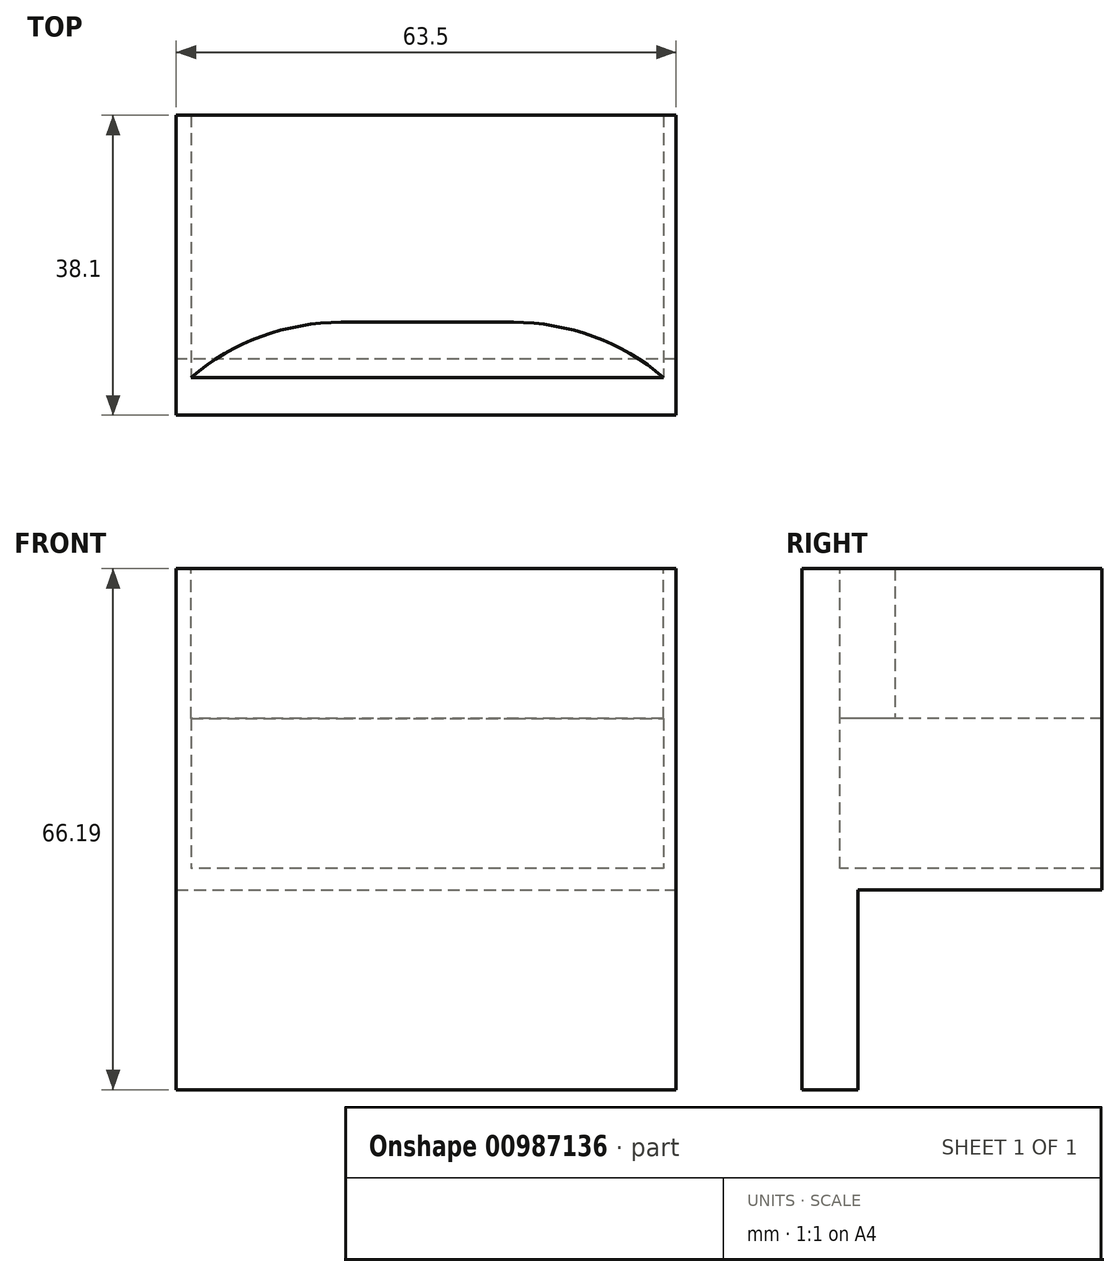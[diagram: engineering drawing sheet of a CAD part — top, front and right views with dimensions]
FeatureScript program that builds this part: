
annotation { "Feature Type Name" : "Feature", "Feature Type Description" : "" }
export const myFeature = defineFeature(function(context is Context, id is Id, definition is map)
    precondition{}
    {
        {
            var Q0;
            Q0=qCreatedBy(makeId("Top.planeOp"),FACE);
            var sketch = newSketch(context, id + "F0", { "sketchPlane" : qUnion([Q0])});
            skLineSegment(sketch, "E0.bottom", {"start": v(-32.48, 36.7) * mm, "end": v(31.02, 36.7) * mm});
            skLineSegment(sketch, "E0.top", {"start": v(-32.48, -26.8) * mm, "end": v(31.02, -26.8) * mm});
            skLineSegment(sketch, "E0.left", {"start": v(-32.48, 36.7) * mm, "end": v(-32.48, -26.8) * mm});
            skLineSegment(sketch, "E0.right", {"start": v(31.02, 36.7) * mm, "end": v(31.02, -26.8) * mm});
            skSolve(sketch);
        }
        {
            var Q0;
            Q0=makeQuery(id+"F0.imprint","IMPRINT",FACE,{"disambiguationData":[TD([[makeQuery(id+"F0.imprint","IMPRINT",EDGE,{"derivedFrom":sQuery(id+"F0.wireOp",EDGE,"E0.bottom")}),-1.0]])]});
            extrude(context, id + "F1", {"entities" : qUnion([Q0]), "depth" : 38.1 * mm, "offsetDistance" : 25.4 * mm});
        }
        {
            var Q0;
            Q0=makeQuery(id+"F0.imprint","IMPRINT",FACE,{"disambiguationData":[TD([[makeQuery(id+"F0.imprint","IMPRINT",EDGE,{"derivedFrom":sQuery(id+"F0.wireOp",EDGE,"E0.bottom")}),-1.0]])]});
            extrude(context, id + "F2", {"entities" : qUnion([Q0]), "operationType" : NewBodyOperationType.ADD, "depth" : 58.42 * mm, "offsetDistance" : 25.4 * mm});
        }
        {
            var Q0;
            Q0=makeQuery(id+"F2.opExtrude","CAP_FACE",FACE,{"disambiguationData":[OSD([sQuery(id+"F0.wireOp",EDGE,"E0.bottom"),sQuery(id+"F0.wireOp",EDGE,"E0.top"),sQuery(id+"F0.wireOp",EDGE,"E0.left"),sQuery(id+"F0.wireOp",EDGE,"E0.right")])],"isStart":false});
            var sketch = newSketch(context, id + "F3", { "sketchPlane" : qUnion([Q0])});
            skLineSegment(sketch, "E1.bottom", {"start": v(-30.58, 10.4) * mm, "end": v(29.42, 10.4) * mm});
            skLineSegment(sketch, "E1.top", {"start": v(-30.58, 3.4) * mm, "end": v(29.42, 3.4) * mm});
            skLineSegment(sketch, "E1.left", {"start": v(-30.58, 10.4) * mm, "end": v(-30.58, 3.4) * mm});
            skLineSegment(sketch, "E1.right", {"start": v(29.42, 10.4) * mm, "end": v(29.42, 3.4) * mm});
            skSolve(sketch);
        }
        {
            var Q0;
            Q0=makeQuery(id+"F3.imprint","IMPRINT",FACE,{"disambiguationData":[TD([[makeQuery(id+"F3.imprint","IMPRINT",EDGE,{"derivedFrom":sQuery(id+"F3.wireOp",EDGE,"E1.bottom")}),-1.0]])]});
            extrude(context, id + "F4", {"entities" : qUnion([Q0]), "operationType" : NewBodyOperationType.REMOVE, "oppositeDirection" : true, "depth" : 38.1 * mm, "offsetDistance" : 25.4 * mm});
        }
        {
            var Q0;
            Q0=makeQuery(id+"F4.boolean.opBoolean","COPY",FACE,{"derivedFrom":makeQuery(id+"F4.opExtrude","SWEPT_FACE",FACE,{"disambiguationData":[OSD([sQuery(id+"F3.wireOp",EDGE,"E1.bottom")])]})});
            var sketch = newSketch(context, id + "F5", { "sketchPlane" : qUnion([Q0])});
            skLineSegment(sketch, "E2.bottom", {"start": v(-30.58, 39.37) * mm, "end": v(29.42, 39.37) * mm});
            skLineSegment(sketch, "E2.top", {"start": v(-30.58, 20.32) * mm, "end": v(29.42, 20.32) * mm});
            skLineSegment(sketch, "E2.left", {"start": v(-30.58, 39.37) * mm, "end": v(-30.58, 20.32) * mm});
            skLineSegment(sketch, "E2.right", {"start": v(29.42, 39.37) * mm, "end": v(29.42, 20.32) * mm});
            skSolve(sketch);
        }
        {
            var Q0;
            Q0=makeQuery(id+"F5.imprint","IMPRINT",FACE,{"disambiguationData":[TD([[makeQuery(id+"F5.imprint","IMPRINT",EDGE,{"derivedFrom":sQuery(id+"F5.wireOp",EDGE,"E2.bottom")}),-1.0]])]});
            extrude(context, id + "F6", {"entities" : qUnion([Q0]), "operationType" : NewBodyOperationType.REMOVE, "oppositeDirection" : true, "depth" : 50.8 * mm, "offsetDistance" : 25.4 * mm});
        }
        {
            var Q0;
            {var subQ0=sQuery(id+"F0.wireOp",EDGE,"E0.top");Q0=makeQuery(id+"F2.boolean.opBoolean","MERGE",FACE,{"derivedFrom":[makeQuery(id+"F1.opExtrude","SWEPT_FACE",FACE,{"disambiguationData":[OSD([subQ0])]}),makeQuery(id+"F2.opExtrude","SWEPT_FACE",FACE,{"disambiguationData":[OSD([subQ0])]})]});}
            extrude(context, id + "F7", {"entities" : qUnion([Q0]), "operationType" : NewBodyOperationType.REMOVE, "oppositeDirection" : true, "depth" : 25.4 * mm, "offsetDistance" : 25.4 * mm});
        }
        {
            var Q0;
            {var subQ0=sQuery(id+"F0.wireOp",EDGE,"E0.right");Q0=makeQuery(id+"F2.boolean.opBoolean","MERGE",FACE,{"derivedFrom":[makeQuery(id+"F1.opExtrude","SWEPT_FACE",FACE,{"disambiguationData":[OSD([subQ0])]}),makeQuery(id+"F2.opExtrude","SWEPT_FACE",FACE,{"disambiguationData":[OSD([subQ0])]})]});}
            var sketch = newSketch(context, id + "F8", { "sketchPlane" : qUnion([Q0])});
            skLineSegment(sketch, "E3", {"start": v(36.7, 17.63) * mm, "end": v(-1.4, 17.63) * mm});
            skSolve(sketch);
        }
        {
            var Q0;
            {var subQ0=sQuery(id+"F8.wireOp",EDGE,"E3");Q0=makeQuery(id+"F8.imprint","IMPRINT",FACE,{"disambiguationData":[TD([[makeQuery(id+"F8.imprint","IMPRINT",EDGE,{"derivedFrom":subQ0}),1.0]])]});}
            extrude(context, id + "F9", {"entities" : qUnion([Q0]), "operationType" : NewBodyOperationType.REMOVE, "oppositeDirection" : true, "depth" : 76.2 * mm, "offsetDistance" : 25.4 * mm});
        }
        {
            var Q0;
            Q0=makeQuery(id+"F4.boolean.opBoolean","COPY",EDGE,{"derivedFrom":makeQuery(id+"F4.opExtrude","SWEPT_EDGE",EDGE,{"disambiguationData":[OSD([sQuery(id+"F3.wireOp",EDGE,"E1.bottom"),sQuery(id+"F3.wireOp",EDGE,"E1.right")])]})});
            var Q1;
            Q1=makeQuery(id+"F4.boolean.opBoolean","COPY",EDGE,{"derivedFrom":makeQuery(id+"F4.opExtrude","SWEPT_EDGE",EDGE,{"disambiguationData":[OSD([sQuery(id+"F3.wireOp",EDGE,"E1.bottom"),sQuery(id+"F3.wireOp",EDGE,"E1.left")])]})});
            fillet(context, id + "F10", {"entities" : qUnion([Q0, Q1]), "radius" : 29.43 * mm, "tangentPropagation" : true, "allowEdgeOverflow" : false});
        }
        {
            var Q0;
            Q0=makeQuery(id+"F9.boolean.opBoolean","COPY",FACE,{"derivedFrom":makeQuery(id+"F9.opExtrude","SWEPT_FACE",FACE,{"disambiguationData":[OSD([sQuery(id+"F8.wireOp",EDGE,"E3")])]})});
            var sketch = newSketch(context, id + "F11", { "sketchPlane" : qUnion([Q0])});
            skLineSegment(sketch, "E4.bottom", {"start": v(31.02, -12.05) * mm, "end": v(-32.67, -12.05) * mm});
            skLineSegment(sketch, "E4.top", {"start": v(31.02, 1.4) * mm, "end": v(-32.67, 1.4) * mm});
            skLineSegment(sketch, "E4.left", {"start": v(31.02, -12.05) * mm, "end": v(31.02, 1.4) * mm});
            skLineSegment(sketch, "E4.right", {"start": v(-32.67, -12.05) * mm, "end": v(-32.67, 1.4) * mm});
            skSolve(sketch);
        }
        {
            var Q0;
            {var subQ0=sQuery(id+"F11.wireOp",EDGE,"E4.left");Q0=makeQuery(id+"F11.imprint","IMPRINT",FACE,{"disambiguationData":[TD([[makeQuery(id+"F11.imprint","IMPRINT",EDGE,{"derivedFrom":subQ0}),1.0]])]});}
            extrude(context, id + "F12", {"entities" : qUnion([Q0]), "operationType" : NewBodyOperationType.ADD, "depth" : 25.4 * mm, "offsetDistance" : 25.4 * mm});
        }
        {
            var Q0;
            Q0=makeQuery(id+"F12.opExtrude","SWEPT_FACE",FACE,{"disambiguationData":[OSD([sQuery(id+"F11.wireOp",EDGE,"E4.bottom")])]});
            extrude(context, id + "F13", {"entities" : qUnion([Q0]), "operationType" : NewBodyOperationType.REMOVE, "oppositeDirection" : true, "depth" : 6.35 * mm, "offsetDistance" : 25.4 * mm});
        }
    });
